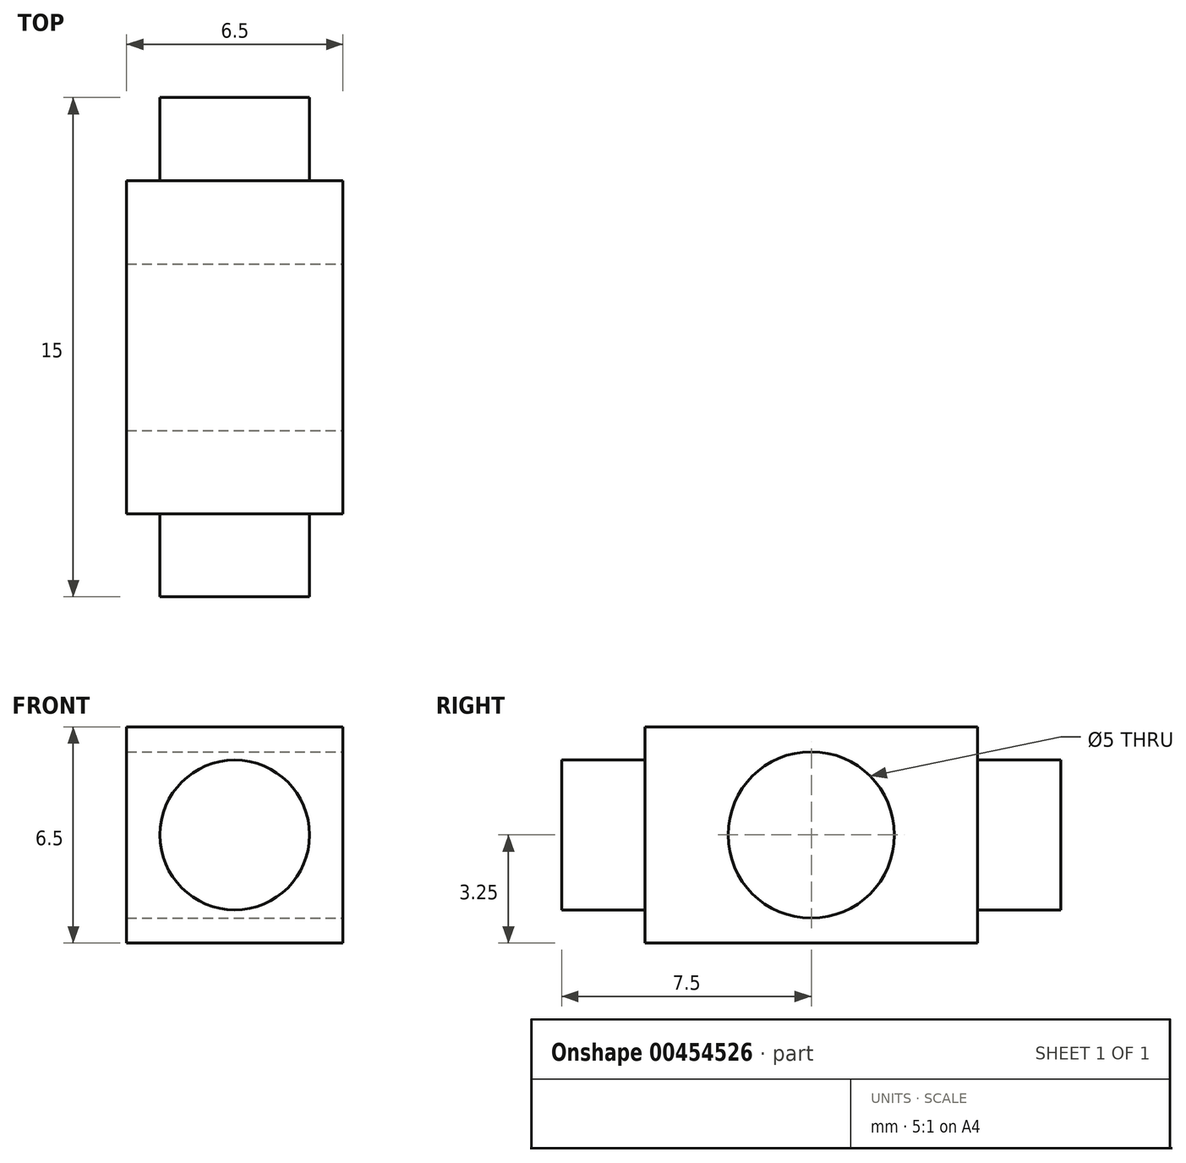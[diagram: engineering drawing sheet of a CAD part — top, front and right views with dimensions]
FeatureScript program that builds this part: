
annotation { "Feature Type Name" : "Feature", "Feature Type Description" : "" }
export const myFeature = defineFeature(function(context is Context, id is Id, definition is map)
    precondition{}
    {
        {
            var Q0;
            Q0=qCreatedBy(makeId("Front.planeOp"),FACE);
            var sketch = newSketch(context, id + "F0", { "sketchPlane" : qUnion([Q0])});
            skLineSegment(sketch, "E0.bottom", {"start": v(0, 0) * mm, "end": v(6.5, 0) * mm});
            skLineSegment(sketch, "E0.top", {"start": v(0, 6.5) * mm, "end": v(6.5, 6.5) * mm});
            skLineSegment(sketch, "E0.left", {"start": v(0, 0) * mm, "end": v(0, 6.5) * mm});
            skLineSegment(sketch, "E0.right", {"start": v(6.5, 0) * mm, "end": v(6.5, 6.5) * mm});
            skSolve(sketch);
        }
        {
            var Q0;
            Q0=makeQuery(id+"F0.imprint","IMPRINT",FACE,{"disambiguationData":[TD([[makeQuery(id+"F0.imprint","IMPRINT",EDGE,{"derivedFrom":sQuery(id+"F0.wireOp",EDGE,"E0.bottom")}),1.0]])]});
            extrude(context, id + "F1", {"entities" : qUnion([Q0]), "depth" : 10 * mm});
        }
        {
            var Q0;
            Q0=makeQuery(id+"F1.opExtrude","CAP_FACE",FACE,{"disambiguationData":[OSD([sQuery(id+"F0.wireOp",EDGE,"E0.bottom"),sQuery(id+"F0.wireOp",EDGE,"E0.top"),sQuery(id+"F0.wireOp",EDGE,"E0.left"),sQuery(id+"F0.wireOp",EDGE,"E0.right")])],"isStart":false});
            var sketch = newSketch(context, id + "F2", { "sketchPlane" : qUnion([Q0])});
            skCircle(sketch, "E1", {"center": v(3.25, 3.25) * mm, "radius": 2.25 * mm});
            skPoint(sketch, "E1.centerSnap0", {"position": v(6.5, 3.25) * mm});
            skPoint(sketch, "E1.centerSnap1", {"position": v(3.25, 6.5) * mm});
            skSolve(sketch);
        }
        {
            var Q0;
            Q0 = qSketchRegion(id + "F2", true);
            extrude(context, id + "F3", {"entities" : qUnion([Q0]), "operationType" : NewBodyOperationType.ADD, "depth" : 2.5 * mm, "hasSecondDirection" : true, "secondDirectionOppositeDirection" : true, "secondDirectionDepth" : 12.5 * mm});
        }
        {
            var Q0;
            Q0=makeQuery(id+"F1.opExtrude","SWEPT_FACE",FACE,{"disambiguationData":[OSD([sQuery(id+"F0.wireOp",EDGE,"E0.right")])]});
            var sketch = newSketch(context, id + "F4", { "sketchPlane" : qUnion([Q0])});
            skCircle(sketch, "E2", {"center": v(-5, 3.25) * mm, "radius": 2.5 * mm});
            skPoint(sketch, "E2.centerSnap0", {"position": v(-10, 3.25) * mm});
            skPoint(sketch, "E2.centerSnap1", {"position": v(-5, 6.5) * mm});
            skSolve(sketch);
        }
        {
            var Q0;
            Q0 = qSketchRegion(id + "F4", true);
            extrude(context, id + "F5", {"entities" : qUnion([Q0]), "operationType" : NewBodyOperationType.REMOVE, "oppositeDirection" : true, "depth" : 25 * mm});
        }
    });
